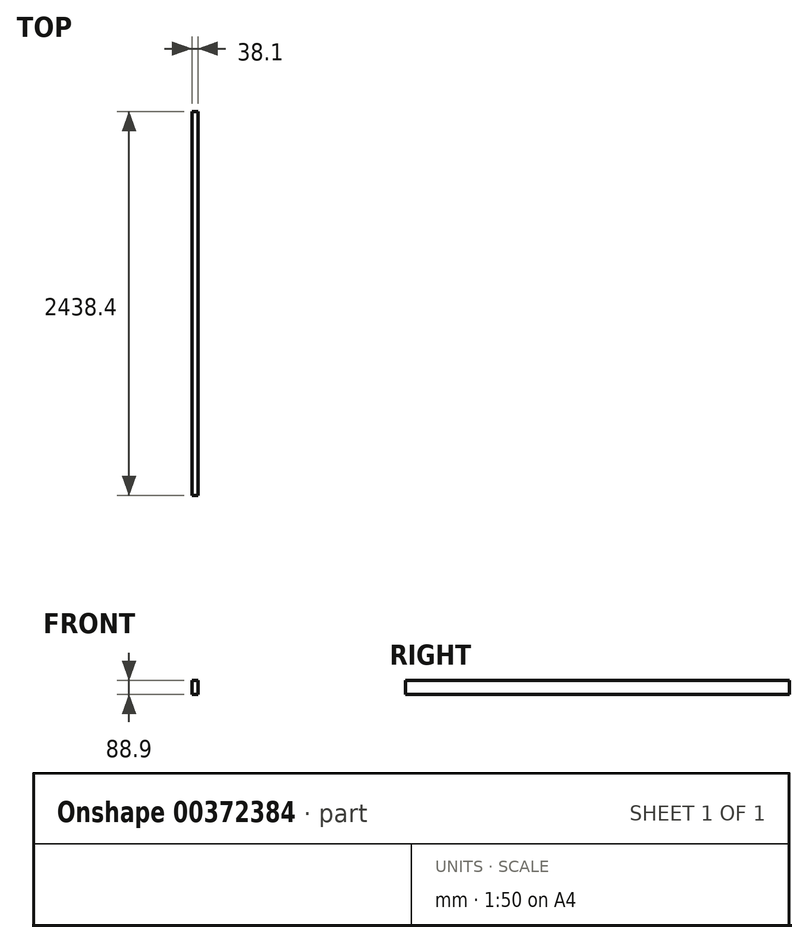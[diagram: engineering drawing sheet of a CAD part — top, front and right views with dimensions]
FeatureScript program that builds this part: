
annotation { "Feature Type Name" : "Feature", "Feature Type Description" : "" }
export const myFeature = defineFeature(function(context is Context, id is Id, definition is map)
    precondition{}
    {
        {
            var Q0;
            Q0=qCreatedBy(makeId("Front.planeOp"),FACE);
            var sketch = newSketch(context, id + "F0", { "sketchPlane" : qUnion([Q0])});
            skLineSegment(sketch, "E0.bottom", {"start": v(-19.05, 44.45) * mm, "end": v(19.05, 44.45) * mm});
            skLineSegment(sketch, "E0.top", {"start": v(-19.05, -44.45) * mm, "end": v(19.05, -44.45) * mm});
            skLineSegment(sketch, "E0.left", {"start": v(-19.05, 44.45) * mm, "end": v(-19.05, -44.45) * mm});
            skLineSegment(sketch, "E0.right", {"start": v(19.05, 44.45) * mm, "end": v(19.05, -44.45) * mm});
            skPoint(sketch, "E0.middle", {"position": v(0, 0) * mm});
            skSolve(sketch);
        }
        {
            var Q0;
            Q0=qSketchRegion(id+"F0",true);
            extrude(context, id + "F1", {"entities" : qUnion([Q0]), "endBound" : BoundingType.SYMMETRIC, "oppositeDirection" : true, "depth" : 2438.4 * mm});
        }
    });
